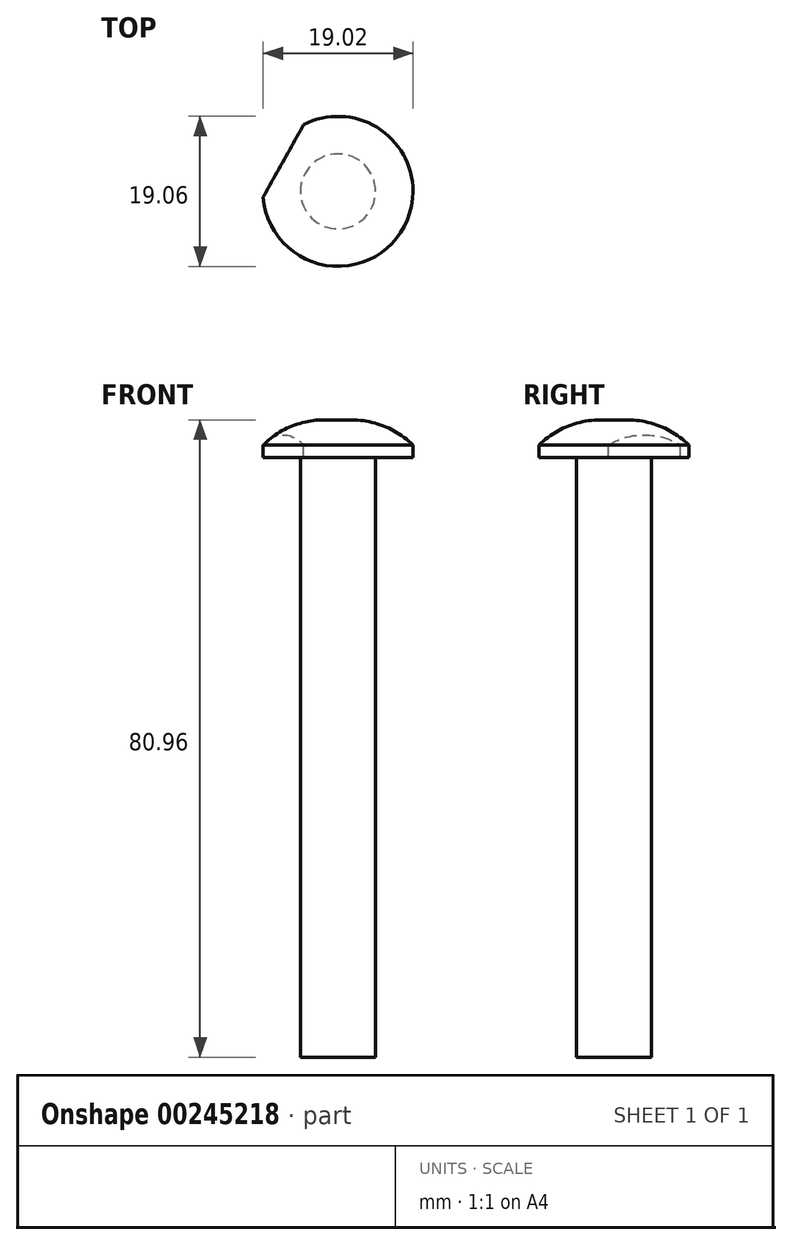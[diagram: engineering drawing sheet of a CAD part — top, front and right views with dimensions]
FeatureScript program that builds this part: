
annotation { "Feature Type Name" : "Feature", "Feature Type Description" : "" }
export const myFeature = defineFeature(function(context is Context, id is Id, definition is map)
    precondition{}
    {
        {
            var Q0;
            Q0=qCreatedBy(makeId("Front.planeOp"),FACE);
            var sketch = newSketch(context, id + "F0", { "sketchPlane" : qUnion([Q0])});
            skLineSegment(sketch, "E0", {"start": v(-551.67, -333.5) * mm, "end": v(-551.67, -257.3) * mm});
            skLineSegment(sketch, "E1", {"start": v(-551.67, -257.3) * mm, "end": v(-556.44, -257.3) * mm});
            skLineSegment(sketch, "E2", {"start": v(-556.44, -257.3) * mm, "end": v(-556.44, -333.5) * mm});
            skLineSegment(sketch, "E3", {"start": v(-556.44, -333.5) * mm, "end": v(-551.67, -333.5) * mm});
            skLineSegment(sketch, "E4", {"start": v(-556.44, -257.3) * mm, "end": v(-556.44, -255.7) * mm});
            skLineSegment(sketch, "E5", {"start": v(-556.44, -255.7) * mm, "end": v(-546.91, -255.7) * mm});
            skLineSegment(sketch, "E6", {"start": v(-546.91, -255.7) * mm, "end": v(-546.91, -257.3) * mm});
            skLineSegment(sketch, "E7", {"start": v(-546.91, -257.3) * mm, "end": v(-551.67, -257.3) * mm});
            skLineSegment(sketch, "E8", {"start": v(-556.44, -255.7) * mm, "end": v(-556.44, -252.53) * mm});
            skLineSegment(sketch, "E9", {"start": v(-556.44, -252.53) * mm, "end": v(-554.72, -252.53) * mm});
            skPoint(sketch, "E10.visualSharp", {"position": v(-549.78, -252.53) * mm});
            skArc(sketch, "E10.filletArc", {"start": v(-546.91, -255.73) * mm, "mid": v(-550.5, -253.36) * mm, "end": v(-554.72, -252.53) * mm});
            skSolve(sketch);
        }
        {
            var Q0;
            Q0=makeQuery(id+"F0.imprint","IMPRINT",FACE,{"disambiguationData":[TD([[makeQuery(id+"F0.imprint","IMPRINT",EDGE,{"derivedFrom":sQuery(id+"F0.wireOp",EDGE,"E0")}),1.0]])]});
            var Q1;
            Q1=makeQuery(id+"F0.imprint","IMPRINT",FACE,{"disambiguationData":[TD([[makeQuery(id+"F0.imprint","IMPRINT",EDGE,{"derivedFrom":sQuery(id+"F0.wireOp",EDGE,"E1")}),-1.0]])]});
            var Q2;
            {var subQ0=sQuery(id+"F0.wireOp",EDGE,"E8");Q2=makeQuery(id+"F0.imprint","IMPRINT",FACE,{"disambiguationData":[TD([[makeQuery(id+"F0.imprint","IMPRINT",EDGE,{"derivedFrom":subQ0}),-1.0]])]});}
            var Q3;
            Q3=sQuery(id+"F0.wireOp",EDGE,"E2");
            revolve(context, id + "F1", {"entities" : qUnion([Q0, Q1, Q2]), "axis" : qUnion([Q3]), "revolveType" : RevolveType.FULL});
        }
        {
            var Q0;
            Q0=makeQuery(id+"F1.opRevolve","SWEPT_FACE",FACE,{"disambiguationData":[OSD([sQuery(id+"F0.wireOp",EDGE,"E9")])]});
            var sketch = newSketch(context, id + "F2", { "sketchPlane" : qUnion([Q0])});
            skCircle(sketch, "E11", {"center": v(-556.44, 0) * mm, "radius": 7.94 * mm});
            skLineSegment(sketch, "E12", {"start": v(-556.44, 0) * mm, "end": v(-563.36, 3.88) * mm});
            skLineSegment(sketch, "E13", {"start": v(-563.36, 3.88) * mm, "end": v(-559.1, 11.5) * mm});
            skLineSegment(sketch, "E14", {"start": v(-559.1, 11.5) * mm, "end": v(-567.56, -3.63) * mm});
            skLineSegment(sketch, "E15", {"start": v(-567.56, -3.63) * mm, "end": v(-570.23, -2.13) * mm});
            skLineSegment(sketch, "E16", {"start": v(-570.23, -2.13) * mm, "end": v(-561.74, 13.04) * mm});
            skLineSegment(sketch, "E17", {"start": v(-561.74, 13.04) * mm, "end": v(-559.1, 11.5) * mm});
            skSolve(sketch);
        }
        {
            var Q0;
            {var subQ0=sQuery(id+"F2.wireOp",EDGE,"E15");Q0=makeQuery(id+"F2.imprint","IMPRINT",FACE,{"disambiguationData":[TD([[makeQuery(id+"F2.imprint","IMPRINT",EDGE,{"derivedFrom":subQ0}),-1.0]])]});}
            extrude(context, id + "F3", {"entities" : qUnion([Q0]), "operationType" : NewBodyOperationType.REMOVE, "endBound" : BoundingType.THROUGH_ALL, "oppositeDirection" : true, "depth" : 25.4 * mm});
        }
    });
